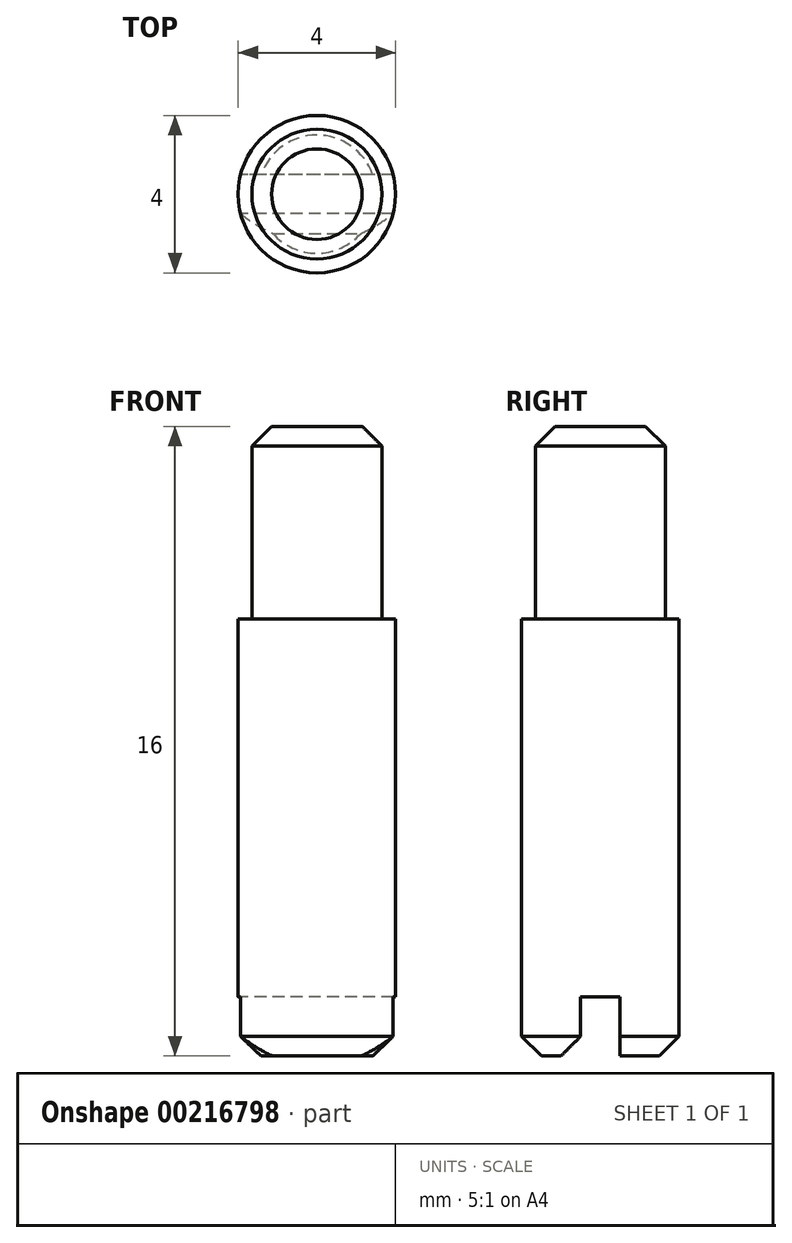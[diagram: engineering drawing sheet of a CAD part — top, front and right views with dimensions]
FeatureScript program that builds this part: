
annotation { "Feature Type Name" : "Feature", "Feature Type Description" : "" }
export const myFeature = defineFeature(function(context is Context, id is Id, definition is map)
    precondition{}
    {
        {
            var Q0;
            Q0=qCreatedBy(makeId("Top.planeOp"),FACE);
            var sketch = newSketch(context, id + "F0", { "sketchPlane" : qUnion([Q0])});
            skCircle(sketch, "E0", {"center": v(0, 0) * mm, "radius": 2 * mm});
            skCircle(sketch, "E1", {"center": v(0, 0) * mm, "radius": 1.65 * mm});
            skSolve(sketch);
        }
        {
            var Q0;
            Q0=makeQuery(id+"F0.imprint","IMPRINT",FACE,{"disambiguationData":[TD([[makeQuery(id+"F0.imprint","IMPRINT",EDGE,{"derivedFrom":sQuery(id+"F0.wireOp",EDGE,"E1")}),1.0]])]});
            extrude(context, id + "F1", {"entities" : qUnion([Q0]), "depth" : 4.9 * mm});
        }
        {
            var Q0;
            Q0=makeQuery(id+"F0.imprint","IMPRINT",FACE,{"disambiguationData":[TD([[makeQuery(id+"F0.imprint","IMPRINT",EDGE,{"derivedFrom":sQuery(id+"F0.wireOp",EDGE,"E1")}),1.0]])]});
            var Q1;
            Q1=makeQuery(id+"F0.imprint","IMPRINT",FACE,{"disambiguationData":[TD([[makeQuery(id+"F0.imprint","IMPRINT",EDGE,{"derivedFrom":sQuery(id+"F0.wireOp",EDGE,"E0")}),1.0]])]});
            extrude(context, id + "F2", {"entities" : qUnion([Q0, Q1]), "operationType" : NewBodyOperationType.ADD, "oppositeDirection" : true, "depth" : 11.1 * mm});
        }
        {
            var Q0;
            Q0=makeQuery(id+"F1.opExtrude","CAP_EDGE",EDGE,{"disambiguationData":[OSD([sQuery(id+"F0.wireOp",EDGE,"E1")])],"isStart":false});
            var Q1;
            Q1=makeQuery(id+"F2.opExtrude","CAP_EDGE",EDGE,{"disambiguationData":[OSD([sQuery(id+"F0.wireOp",EDGE,"E0")])],"isStart":false});
            chamfer(context, id + "F3", {"entities" : qUnion([Q0, Q1]), "width" : 0.5 * mm, "tangentPropagation" : true});
        }
        {
            var Q0;
            Q0=makeQuery(id+"F2.opExtrude","CAP_FACE",FACE,{"disambiguationData":[OSD([sQuery(id+"F0.wireOp",EDGE,"E0")])],"isStart":false});
            var sketch = newSketch(context, id + "F4", { "sketchPlane" : qUnion([Q0])});
            skLineSegment(sketch, "E2.bottom", {"start": v(2, 0.5) * mm, "end": v(-2, 0.5) * mm});
            skLineSegment(sketch, "E2.top", {"start": v(2, -0.5) * mm, "end": v(-2, -0.5) * mm});
            skLineSegment(sketch, "E2.left", {"start": v(2, 0.5) * mm, "end": v(2, -0.5) * mm});
            skLineSegment(sketch, "E2.right", {"start": v(-2, 0.5) * mm, "end": v(-2, -0.5) * mm});
            skPoint(sketch, "E2.middle", {"position": v(0, 0) * mm});
            skSolve(sketch);
        }
        {
            var Q0;
            Q0 = qSketchRegion(id + "F4", true);
            extrude(context, id + "F5", {"entities" : qUnion([Q0]), "operationType" : NewBodyOperationType.REMOVE, "oppositeDirection" : true, "depth" : 1.5 * mm});
        }
        {
            var Q0;
            Q0=makeQuery(id+"F5.boolean.opBoolean","COPY",EDGE,{"derivedFrom":makeQuery(id+"F5.opExtrude","CAP_EDGE",EDGE,{"disambiguationData":[OSD([sQuery(id+"F4.wireOp",EDGE,"E2.top")])],"isStart":true})});
            var Q1;
            Q1=makeQuery(id+"F5.boolean.opBoolean","COPY",EDGE,{"derivedFrom":makeQuery(id+"F5.opExtrude","CAP_EDGE",EDGE,{"disambiguationData":[OSD([sQuery(id+"F4.wireOp",EDGE,"E2.bottom")])],"isStart":true})});
            chamfer(context, id + "F6", {"entities" : qUnion([Q0, Q1]), "width" : 0.5 * mm, "tangentPropagation" : true});
        }
    });
